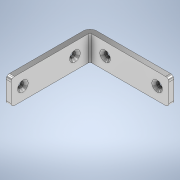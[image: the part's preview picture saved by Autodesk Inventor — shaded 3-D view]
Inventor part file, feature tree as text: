
AUTODESK INVENTOR PART (.ipt)
format: ipt  version: 2021 (Build 250183000, 183)  size: 145,920 bytes
history: native  units: mm
features: sketch x3, hole x2, extrude x1, fillet x1, projected_geometry x1
ambient origin geometry x8: Origin, YZ Plane, XZ Plane, XY Plane, X Axis, Y Axis, Z Axis, Center Point
bodies: Solid1 (feature_tree)
feature tree (8):
  extrude  "Extrusion1"  Depth=50.0mm
  fillet  "Fillet1"  Radius=4.0mm
  hole  "Hole1"  [1 undecoded]
  hole  "Hole2"  [1 undecoded]
  sketch  "Sketch1"  dims[d0=50.0mm d1=50.0mm d2=4.0mm]
  sketch  "Sketch2"  dims[d3=47.0mm d4=47.0mm]
  sketch  "Sketch3"  dims[d5=1.0mm d6=15.0mm d7=0.0mm d8=2.0mm d9=7.0mm d10=31.0mm d11=3.5mm d12=8.0mm d13=6.3mm d14=2.0mm d15=90.0deg d16=9.0mm d17=20.594885mm d18=7.0mm d19=31.0mm d20=3.5mm d21=8.0mm d22=6.3mm d23=2.0mm d24=90.0deg d25=9.0mm d26=20.594885mm]
  projected_geometry  "Projected Loop1"
note: 2 required parameter values undecoded (feature->parameter linkage not recoverable at this tier; creation-order binding heuristic only, values carry confidence <= 0.55)
